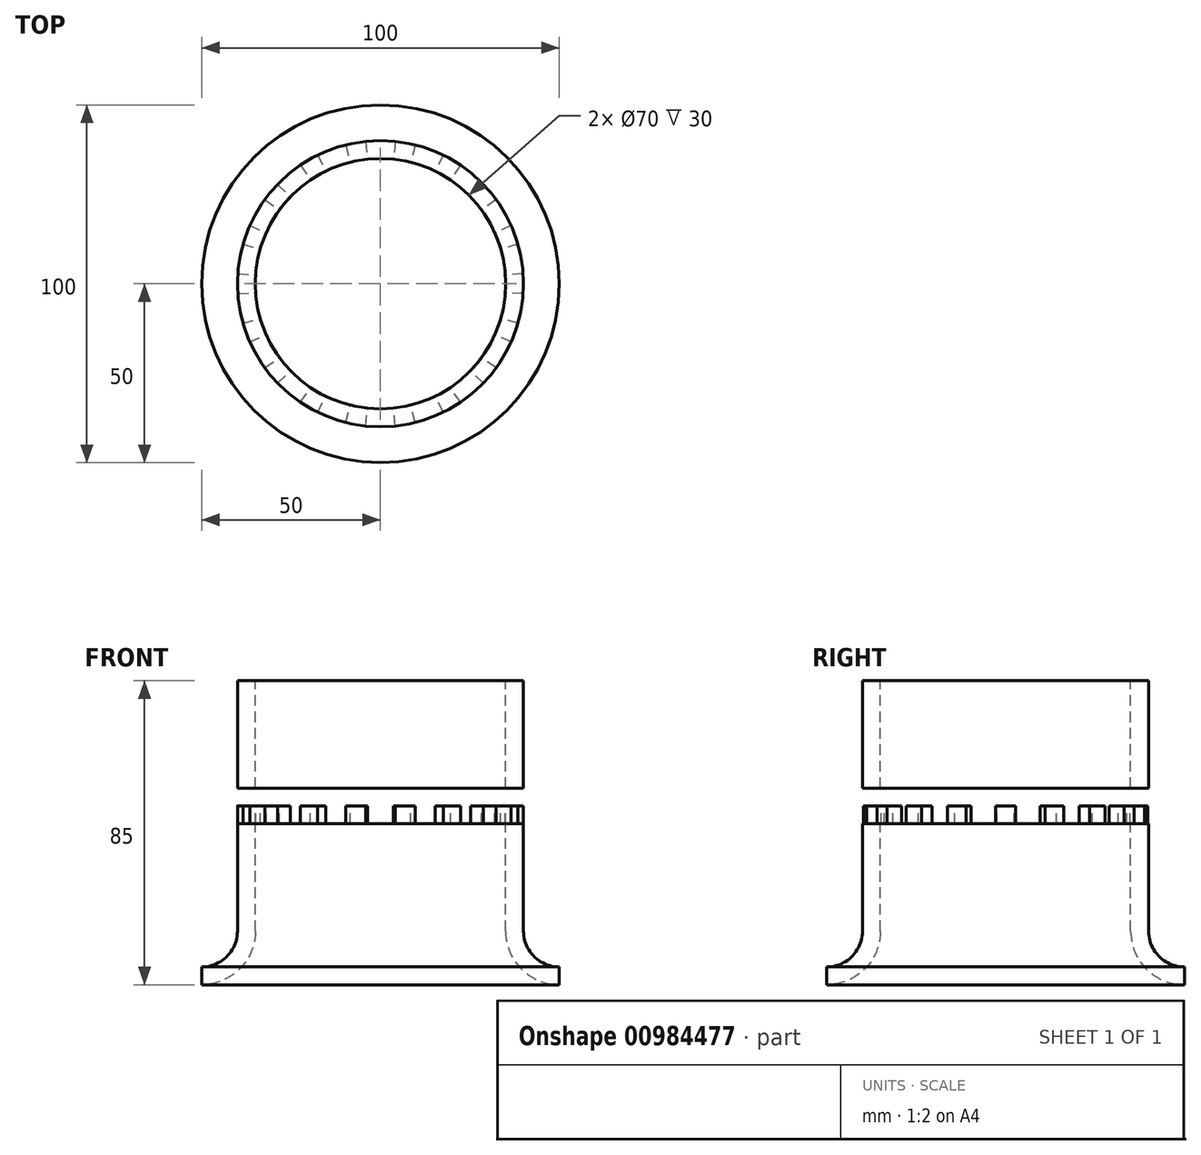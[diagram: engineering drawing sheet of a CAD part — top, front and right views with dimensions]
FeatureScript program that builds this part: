
annotation { "Feature Type Name" : "Feature", "Feature Type Description" : "" }
export const myFeature = defineFeature(function(context is Context, id is Id, definition is map)
    precondition{}
    {
        {
            var Q0;
            Q0=qCreatedBy(makeId("Front.planeOp"),FACE);
            var sketch = newSketch(context, id + "F0", { "sketchPlane" : qUnion([Q0])});
            skLineSegment(sketch, "E0.bottom", {"start": v(-40, 0) * mm, "end": v(-35, 0) * mm});
            skLineSegment(sketch, "E0.top", {"start": v(-40, 70) * mm, "end": v(-35, 70) * mm});
            skLineSegment(sketch, "E0.left", {"start": v(-40, 0) * mm, "end": v(-40, 70) * mm});
            skLineSegment(sketch, "E0.right", {"start": v(-35, 0) * mm, "end": v(-35, 70) * mm});
            skLineSegment(sketch, "E1.left", {"start": v(-35, 70) * mm, "end": v(-35, 65) * mm});
            skPoint(sketch, "E2", {"position": v(-50, -10) * mm});
            skArc(sketch, "E3", {"start": v(-50, -10) * mm, "mid": v(-42.93, -7.07) * mm, "end": v(-40, 0) * mm});
            skArc(sketch, "E4.0", {"start": v(-50, -15) * mm, "mid": v(-39.4, -10.6) * mm, "end": v(-35, 0) * mm});
            skLineSegment(sketch, "E5", {"start": v(-50, -10) * mm, "end": v(-50, -15) * mm});
            skLineSegment(sketch, "E6.right", {"start": v(0, 70) * mm, "end": v(0, 65) * mm});
            skLineSegment(sketch, "E7.bottom", {"start": v(-35, 65) * mm, "end": v(-40, 65) * mm});
            skLineSegment(sketch, "E7.top", {"start": v(-35, 60) * mm, "end": v(-40, 60) * mm});
            skLineSegment(sketch, "E7.left", {"start": v(-35, 65) * mm, "end": v(-35, 60) * mm});
            skLineSegment(sketch, "E7.right", {"start": v(-40, 65) * mm, "end": v(-40, 60) * mm});
            skLineSegment(sketch, "E8.top", {"start": v(-35, 55) * mm, "end": v(-40, 55) * mm});
            skLineSegment(sketch, "E8.left", {"start": v(-35, 60) * mm, "end": v(-35, 55) * mm});
            skLineSegment(sketch, "E8.right", {"start": v(-40, 60) * mm, "end": v(-40, 55) * mm});
            skLineSegment(sketch, "E9.top", {"start": v(-35, 50) * mm, "end": v(-40, 50) * mm});
            skLineSegment(sketch, "E9.left", {"start": v(-35, 55) * mm, "end": v(-35, 50) * mm});
            skLineSegment(sketch, "E9.right", {"start": v(-40, 55) * mm, "end": v(-40, 50) * mm});
            skLineSegment(sketch, "E10.top", {"start": v(-35, 45) * mm, "end": v(-40, 45) * mm});
            skLineSegment(sketch, "E10.left", {"start": v(-35, 50) * mm, "end": v(-35, 45) * mm});
            skLineSegment(sketch, "E10.right", {"start": v(-40, 50) * mm, "end": v(-40, 45) * mm});
            skLineSegment(sketch, "E11.top", {"start": v(-35, 40) * mm, "end": v(-40, 40) * mm});
            skLineSegment(sketch, "E11.left", {"start": v(-35, 45) * mm, "end": v(-35, 40) * mm});
            skLineSegment(sketch, "E11.right", {"start": v(-40, 45) * mm, "end": v(-40, 40) * mm});
            skLineSegment(sketch, "E12", {"start": v(-35, 60) * mm, "end": v(0, 60) * mm});
            skLineSegment(sketch, "E13", {"start": v(-35, 50) * mm, "end": v(0, 50) * mm});
            skLineSegment(sketch, "E14.bottom", {"start": v(-40, 65) * mm, "end": v(0, 65) * mm});
            skLineSegment(sketch, "E14.top", {"start": v(-40, 60) * mm, "end": v(0, 60) * mm});
            skLineSegment(sketch, "E14.right", {"start": v(0, 65) * mm, "end": v(0, 60) * mm});
            skLineSegment(sketch, "E15.bottom", {"start": v(-40, 55) * mm, "end": v(0, 55) * mm});
            skLineSegment(sketch, "E15.top", {"start": v(-40, 50) * mm, "end": v(0, 50) * mm});
            skLineSegment(sketch, "E15.right", {"start": v(0, 55) * mm, "end": v(0, 50) * mm});
            skLineSegment(sketch, "E16.bottom", {"start": v(-40, 45) * mm, "end": v(0, 45) * mm});
            skLineSegment(sketch, "E16.top", {"start": v(-40, 40) * mm, "end": v(0, 40) * mm});
            skLineSegment(sketch, "E16.right", {"start": v(0, 45) * mm, "end": v(0, 40) * mm});
            skLineSegment(sketch, "E17.bottom", {"start": v(0, 65) * mm, "end": v(40, 65) * mm});
            skLineSegment(sketch, "E17.top", {"start": v(0, 60) * mm, "end": v(40, 60) * mm});
            skLineSegment(sketch, "E17.right", {"start": v(40, 65) * mm, "end": v(40, 60) * mm});
            skLineSegment(sketch, "E18.bottom", {"start": v(0, 55) * mm, "end": v(40, 55) * mm});
            skLineSegment(sketch, "E18.top", {"start": v(0, 50) * mm, "end": v(40, 50) * mm});
            skLineSegment(sketch, "E18.right", {"start": v(40, 55) * mm, "end": v(40, 50) * mm});
            skLineSegment(sketch, "E19.bottom", {"start": v(0, 45) * mm, "end": v(40, 45) * mm});
            skLineSegment(sketch, "E19.top", {"start": v(0, 40) * mm, "end": v(40, 40) * mm});
            skLineSegment(sketch, "E19.right", {"start": v(40, 45) * mm, "end": v(40, 40) * mm});
            skLineSegment(sketch, "E20.bottom", {"start": v(-40, 40) * mm, "end": v(-35, 40) * mm});
            skLineSegment(sketch, "E20.top", {"start": v(-40, 35) * mm, "end": v(-35, 35) * mm});
            skLineSegment(sketch, "E20.left", {"start": v(-40, 40) * mm, "end": v(-40, 35) * mm});
            skLineSegment(sketch, "E20.right", {"start": v(-35, 40) * mm, "end": v(-35, 35) * mm});
            skLineSegment(sketch, "E21.top", {"start": v(-40, 30) * mm, "end": v(-35, 30) * mm});
            skLineSegment(sketch, "E21.left", {"start": v(-40, 35) * mm, "end": v(-40, 30) * mm});
            skLineSegment(sketch, "E21.right", {"start": v(-35, 35) * mm, "end": v(-35, 30) * mm});
            skSolve(sketch);
        }
        {
            var Q0;
            Q0=makeQuery(id+"F0.imprint","IMPRINT",FACE,{"disambiguationData":[TD([[makeQuery(id+"F0.imprint","IMPRINT",EDGE,{"derivedFrom":sQuery(id+"F0.wireOp",EDGE,"xu9EFYSj-UlCB-hGFn-sjHT-5frtN7S3sQ2u.bottom")}),-1.0]])]});
            var Q1;
            Q1=makeQuery(id+"F0.imprint","IMPRINT",FACE,{"disambiguationData":[TD([[makeQuery(id+"F0.imprint","IMPRINT",EDGE,{"derivedFrom":sQuery(id+"F0.wireOp",EDGE,"ZhQ0to2A-zMFQ-CqfW-yxqc-obk5LJcw4HI6.bottom")}),-1.0]])]});
            var Q2;
            Q2=makeQuery(id+"F0.imprint","IMPRINT",FACE,{"disambiguationData":[TD([[makeQuery(id+"F0.imprint","IMPRINT",EDGE,{"derivedFrom":sQuery(id+"F0.wireOp",EDGE,"TZdXhDfG-McdC-TP1y-ehiR-sRM3uSC1ZOd2.bottom")}),-1.0]])]});
            var Q3;
            Q3=makeQuery(id+"F0.imprint","IMPRINT",FACE,{"disambiguationData":[TD([[makeQuery(id+"F0.imprint","IMPRINT",EDGE,{"derivedFrom":sQuery(id+"F0.wireOp",EDGE,"E0.bottom")}),1.0]])]});
            var Q4;
            Q4=makeQuery(id+"F0.imprint","IMPRINT",FACE,{"disambiguationData":[TD([[makeQuery(id+"F0.imprint","IMPRINT",EDGE,{"derivedFrom":sQuery(id+"F0.wireOp",EDGE,"E0.bottom")}),-1.0]])]});
            var Q5;
            Q5=makeQuery(id+"F0.imprint","IMPRINT",FACE,{"disambiguationData":[TD([[makeQuery(id+"F0.imprint","IMPRINT",EDGE,{"derivedFrom":sQuery(id+"F0.wireOp",EDGE,"E7.bottom")}),1.0]])]});
            var Q6;
            Q6=makeQuery(id+"F0.imprint","IMPRINT",FACE,{"disambiguationData":[TD([[makeQuery(id+"F0.imprint","IMPRINT",EDGE,{"derivedFrom":sQuery(id+"F0.wireOp",EDGE,"E7.top")}),1.0]])]});
            var Q7;
            Q7=makeQuery(id+"F0.imprint","IMPRINT",FACE,{"disambiguationData":[TD([[makeQuery(id+"F0.imprint","IMPRINT",EDGE,{"derivedFrom":sQuery(id+"F0.wireOp",EDGE,"E8.top")}),1.0]])]});
            var Q8;
            Q8=makeQuery(id+"F0.imprint","IMPRINT",FACE,{"disambiguationData":[TD([[makeQuery(id+"F0.imprint","IMPRINT",EDGE,{"derivedFrom":sQuery(id+"F0.wireOp",EDGE,"E9.top")}),1.0]])]});
            var Q9;
            Q9=makeQuery(id+"F0.imprint","IMPRINT",FACE,{"disambiguationData":[TD([[makeQuery(id+"F0.imprint","IMPRINT",EDGE,{"derivedFrom":sQuery(id+"F0.wireOp",EDGE,"E10.top")}),1.0]])]});
            var Q10;
            Q10=makeQuery(id+"F0.imprint","IMPRINT",FACE,{"disambiguationData":[TD([[makeQuery(id+"F0.imprint","IMPRINT",EDGE,{"derivedFrom":sQuery(id+"F0.wireOp",EDGE,"f1aae11f-0c1b-40a7-95d8-08e4127c4ad611.MirrorCS")}),1.0]])]});
            var Q11;
            {var subQ0=sQuery(id+"F0.wireOp",EDGE,"f1aae11f-0c1b-40a7-95d8-08e4127c4ad612.MirrorCS");Q11=makeQuery(id+"F0.imprint","IMPRINT",FACE,{"disambiguationData":[TD([[makeQuery(id+"F0.imprint","IMPRINT",EDGE,{"derivedFrom":subQ0}),1.0]])]});}
            var Q12;
            {var subQ0=sQuery(id+"F0.wireOp",EDGE,"f1aae11f-0c1b-40a7-95d8-08e4127c4ad612.MirrorCS");Q12=makeQuery(id+"F0.imprint","IMPRINT",FACE,{"disambiguationData":[TD([[makeQuery(id+"F0.imprint","IMPRINT",EDGE,{"derivedFrom":subQ0}),-1.0]])]});}
            var Q13;
            {var subQ0=sQuery(id+"F0.wireOp",EDGE,"f1aae11f-0c1b-40a7-95d8-08e4127c4ad610.MirrorCS");Q13=makeQuery(id+"F0.imprint","IMPRINT",FACE,{"disambiguationData":[TD([[makeQuery(id+"F0.imprint","IMPRINT",EDGE,{"derivedFrom":subQ0}),1.0]])]});}
            var Q14;
            {var subQ0=sQuery(id+"F0.wireOp",EDGE,"f1aae11f-0c1b-40a7-95d8-08e4127c4ad69.MirrorCS");Q14=makeQuery(id+"F0.imprint","IMPRINT",FACE,{"disambiguationData":[TD([[makeQuery(id+"F0.imprint","IMPRINT",EDGE,{"derivedFrom":subQ0}),1.0]])]});}
            var Q15;
            Q15=makeQuery(id+"F0.imprint","IMPRINT",FACE,{"disambiguationData":[TD([[makeQuery(id+"F0.imprint","IMPRINT",EDGE,{"derivedFrom":sQuery(id+"F0.wireOp",EDGE,"f1aae11f-0c1b-40a7-95d8-08e4127c4ad68.MirrorCS")}),1.0]])]});
            var Q16;
            {var subQ0=sQuery(id+"F0.wireOp",EDGE,"E10.left");Q16=makeQuery(id+"F0.imprint","IMPRINT",FACE,{"disambiguationData":[TD([[makeQuery(id+"F0.imprint","IMPRINT",EDGE,{"derivedFrom":subQ0}),-1.0]])]});}
            var Q17;
            {var subQ0=sQuery(id+"F0.wireOp",EDGE,"E8.left");Q17=makeQuery(id+"F0.imprint","IMPRINT",FACE,{"disambiguationData":[TD([[makeQuery(id+"F0.imprint","IMPRINT",EDGE,{"derivedFrom":subQ0}),-1.0]])]});}
            var Q18;
            {var subQ0=sQuery(id+"F0.wireOp",EDGE,"E0.top");Q18=makeQuery(id+"F0.imprint","IMPRINT",FACE,{"disambiguationData":[TD([[makeQuery(id+"F0.imprint","IMPRINT",EDGE,{"derivedFrom":subQ0}),-1.0]])]});}
            var Q19;
            Q19=makeQuery(id+"F0.imprint","IMPRINT",FACE,{"disambiguationData":[TD([[makeQuery(id+"F0.imprint","IMPRINT",EDGE,{"derivedFrom":sQuery(id+"F0.wireOp",EDGE,"E20.bottom")}),-1.0]])]});
            var Q20;
            Q20=sQuery(id+"F0.wireOp",EDGE,"E6.right");
            revolve(context, id + "F1", {"surfaceOperationType" : NewSurfaceOperationType.NEW, "entities" : qUnion([Q0, Q1, Q2, Q3, Q4, Q5, Q6, Q7, Q8, Q9, Q10, Q11, Q12, Q13, Q14, Q15, Q16, Q17, Q18, Q19]), "axis" : qUnion([Q20]), "revolveType" : RevolveType.FULL});
        }
        {
            var Q0;
            {var subQ0=sQuery(id+"F0.wireOp",EDGE,"E11.left");Q0=makeQuery(id+"F0.imprint","IMPRINT",FACE,{"disambiguationData":[TD([[makeQuery(id+"F0.imprint","IMPRINT",EDGE,{"derivedFrom":subQ0}),-1.0]])]});}
            var Q1;
            {var subQ0=sQuery(id+"F0.wireOp",EDGE,"E9.left");Q1=makeQuery(id+"F0.imprint","IMPRINT",FACE,{"disambiguationData":[TD([[makeQuery(id+"F0.imprint","IMPRINT",EDGE,{"derivedFrom":subQ0}),-1.0]])]});}
            var Q2;
            {var subQ0=sQuery(id+"F0.wireOp",EDGE,"E7.left");Q2=makeQuery(id+"F0.imprint","IMPRINT",FACE,{"disambiguationData":[TD([[makeQuery(id+"F0.imprint","IMPRINT",EDGE,{"derivedFrom":subQ0}),-1.0]])]});}
            var Q3;
            Q3=makeQuery(id+"F0.imprint","IMPRINT",FACE,{"disambiguationData":[TD([[makeQuery(id+"F0.imprint","IMPRINT",EDGE,{"derivedFrom":sQuery(id+"F0.wireOp",EDGE,"E20.top")}),-1.0]])]});
            var Q4;
            Q4=sQuery(id+"F0.wireOp",EDGE,"E6.right");
            revolve(context, id + "F2", {"surfaceOperationType" : NewSurfaceOperationType.NEW, "entities" : qUnion([Q0, Q1, Q2, Q3]), "axis" : qUnion([Q4]), "revolveType" : RevolveType.SYMMETRIC, "angle" : 8 * degree});
        }
        {
            var Q0;
            Q0=makeQuery(id+"F2.opRevolve","SWEPT_BODY",BODY,{"disambiguationData":[OSD([sQuery(id+"F0.wireOp",EDGE,"E7.left"),sQuery(id+"F0.wireOp",EDGE,"E14.bottom"),sQuery(id+"F0.wireOp",EDGE,"E14.top"),sQuery(id+"F0.wireOp",EDGE,"E7.right")])]});
            var Q1;
            Q1=makeQuery(id+"F2.opRevolve","SWEPT_BODY",BODY,{"disambiguationData":[OSD([sQuery(id+"F0.wireOp",EDGE,"E9.left"),sQuery(id+"F0.wireOp",EDGE,"E15.bottom"),sQuery(id+"F0.wireOp",EDGE,"E15.top"),sQuery(id+"F0.wireOp",EDGE,"E9.right")])]});
            var Q2;
            Q2=makeQuery(id+"F2.opRevolve","SWEPT_BODY",BODY,{"disambiguationData":[OSD([sQuery(id+"F0.wireOp",EDGE,"E11.left"),sQuery(id+"F0.wireOp",EDGE,"E16.bottom"),sQuery(id+"F0.wireOp",EDGE,"E16.top"),sQuery(id+"F0.wireOp",EDGE,"E11.right")])]});
            var Q3;
            Q3=makeQuery(id+"F2.opRevolve","SWEPT_BODY",BODY,{"disambiguationData":[OSD([sQuery(id+"F0.wireOp",EDGE,"E20.top"),sQuery(id+"F0.wireOp",EDGE,"E21.top"),sQuery(id+"F0.wireOp",EDGE,"E21.left"),sQuery(id+"F0.wireOp",EDGE,"E21.right")])]});
            var Q4;
            Q4=sQuery(id+"F0.wireOp",EDGE,"E6.right");
            circularPattern(context, id + "F3", {"entities" : qUnion([Q0, Q1, Q2, Q3]), "axis" : qUnion([Q4]), "angle" : 360 * degree, "instanceCount" : 18, "equalSpace" : true});
        }
    });
